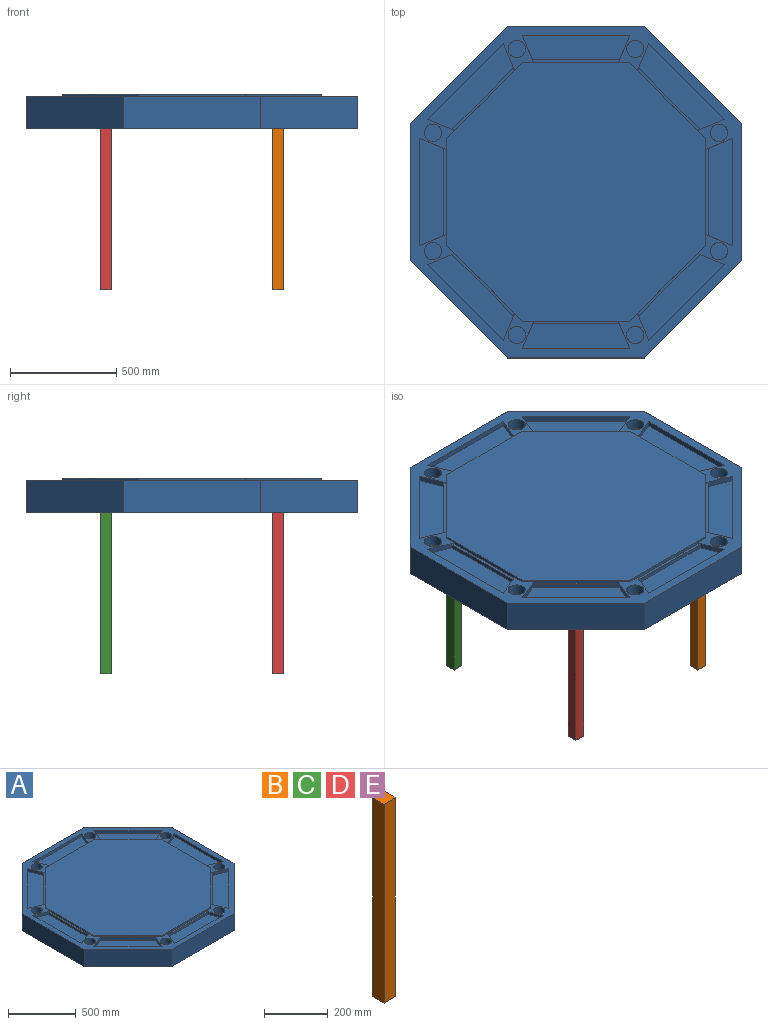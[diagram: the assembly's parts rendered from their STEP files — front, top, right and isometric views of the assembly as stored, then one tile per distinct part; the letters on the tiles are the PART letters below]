
ASSEMBLY  parts=5 mates=4
PART A: 84 faces, bbox 1564.9x1564.9x161.9 mm
  f0: plane 129.64x53.7mm, normal (-0.92,-0.38,0), area 3302.3mm2, adj f1,f9,f13,f61,f81,f83
  f1: plane 407.06x407.06mm, normal (0,0,1), area 53644.2mm2, adj f0,f13,f37,f81,f82
  f2: plane 129.64x53.7mm, normal (-0.38,-0.92,0), area 3302.3mm2, adj f9,f24,f60,f62,f79,f80
  f3: plane 407.06x407.06mm, normal (0,0,1), area 53644.1mm2, adj f10,f34,f35,f77
  f4: plane 129.64x53.7mm, normal (0.92,-0.38,0), area 3302.3mm2, adj f5,f9,f23,f58,f75,f76
  f5: plane 507.17x116.94mm, normal (0,0,1), area 53644.2mm2, adj f4,f23,f33,f75
  f6: plane 507.17x116.94mm, normal (0,0,1), area 53644.1mm2, adj f21,f29,f30,f71
  f7: plane 129.64x53.7mm, normal (-0.38,0.92,0), area 3302.3mm2, adj f9,f11,f55,f64,f69,f70
  f8: plane 129.64x53.7mm, normal (-0.92,0.38,0), area 3302.3mm2, adj f9,f12,f54,f65,f67,f68
  f9: plane 1564.91x1564.91mm, normal (0,0,1), area 285544.7mm2, adj f0,f2,f4,f7,f8,f10,f11,f12
  f10: plane 358.62x358.62mm, normal (0.71,0.71,0), area 12882mm2, adj f3,f9,f34,f35
  f11: plane 358.62x358.62mm, normal (-0.71,-0.71,0), area 12882mm2, adj f7,f9,f28,f64
  f12: plane 507.17x25.4mm, normal (0,-1,0), area 12882mm2, adj f8,f9,f27,f65
  f13: plane 358.62x358.62mm, normal (0.71,-0.71,0), area 12882mm2, adj f0,f1,f9,f37
  f14: plane 458.35x458.35mm, normal (-0.71,0.71,0), area 98786.8mm2, adj f9,f15,f25,f26
  f15: plane 648.21x152.4mm, normal (-1,0,0), area 98786.8mm2, adj f9,f14,f16,f26
  f16: plane 458.35x458.35mm, normal (-0.71,-0.71,0), area 98786.8mm2, adj f9,f15,f17,f26
  f17: plane 648.21x152.4mm, normal (0,-1,0), area 98786.8mm2, adj f9,f16,f18,f26
  f18: plane 458.35x458.35mm, normal (0.71,-0.71,0), area 98786.7mm2, adj f9,f17,f19,f26
  f19: plane 648.21x152.4mm, normal (1,0,0), area 98786.8mm2, adj f9,f18,f20,f26
  f20: plane 458.35x458.35mm, normal (0.71,0.71,0), area 98786.7mm2, adj f9,f19,f25,f26
  f21: plane 507.17x25.4mm, normal (-1,0,0), area 12882mm2, adj f6,f9,f29,f30
  f22: plane 358.62x358.62mm, normal (-0.71,0.71,0), area 12882mm2, adj f9,f31,f32,f63
  f23: plane 507.17x25.4mm, normal (0,1,0), area 12882mm2, adj f4,f5,f9,f33
  f24: plane 507.17x25.4mm, normal (1,0,0), area 12882mm2, adj f2,f9,f36,f62
  f25: plane 648.21x152.4mm, normal (0,1,0), area 98786.8mm2, adj f9,f14,f20,f26
  f26: plane 1564.91x1564.91mm, normal (0,0,-1), area 2028772.5mm2, adj f14,f15,f16,f17,f18,f19,f20,f25
  f27: plane 129.64x53.7mm, normal (0.92,0.38,0), area 3302.3mm2, adj f9,f12,f54,f65,f67,f68
  f28: plane 129.64x53.7mm, normal (0.92,-0.38,0), area 3302.3mm2, adj f9,f11,f55,f64,f69,f70
  f29: plane 129.64x53.7mm, normal (0.38,-0.92,0), area 3302.3mm2, adj f6,f9,f21,f56,f71,f72
  f30: plane 129.64x53.7mm, normal (0.38,0.92,0), area 3302.3mm2, adj f6,f9,f21,f56,f71,f72
  f31: plane 129.64x53.7mm, normal (-0.38,-0.92,0), area 3302.3mm2, adj f9,f22,f57,f63,f73,f74
  f32: plane 129.64x53.7mm, normal (0.92,0.38,0), area 3302.3mm2, adj f9,f22,f57,f63,f73,f74
  f33: plane 129.64x53.7mm, normal (-0.92,-0.38,0), area 3302.3mm2, adj f5,f9,f23,f58,f75,f76
  f34: plane 129.64x53.7mm, normal (-0.92,0.38,0), area 3302.3mm2, adj f3,f9,f10,f59,f77,f78
  f35: plane 129.64x53.7mm, normal (0.38,-0.92,0), area 3302.3mm2, adj f3,f9,f10,f59,f77,f78
  f36: plane 129.64x53.7mm, normal (-0.38,0.92,0), area 3302.3mm2, adj f9,f24,f60,f62,f79,f80
  f37: plane 129.64x53.7mm, normal (0.38,0.92,0), area 3302.3mm2, adj f1,f9,f13,f61,f82,f83
  f38: cylinder r=40.64mm len=81.28mm, axis (0,0,-1), area 12971.7mm2, adj f9,f53
  f39: cylinder r=40.64mm len=81.28mm, axis (0,0,-1), area 12971.7mm2, adj f9,f51
  f40: cylinder r=40.64mm len=81.28mm, axis (0,0,-1), area 12971.7mm2, adj f9,f49
  f41: cylinder r=40.64mm len=81.28mm, axis (0,0,-1), area 12971.7mm2, adj f9,f48
  f42: cylinder r=40.64mm len=81.28mm, axis (0,0,-1), area 12971.7mm2, adj f9,f52
  f43: cylinder r=40.64mm len=81.28mm, axis (0,0,-1), area 12971.7mm2, adj f9,f50
  f44: cylinder r=40.64mm len=81.28mm, axis (0,0,-1), area 12971.7mm2, adj f9,f47
  f45: cylinder r=40.64mm len=81.28mm, axis (0,0,-1), area 12971.7mm2, adj f9,f46
  f46: plane 81.28x81.28mm, normal (0,0,1), area 5188.7mm2, adj f45
  f47: plane 81.28x81.28mm, normal (0,0,1), area 5188.7mm2, adj f44
  f48: plane 81.28x81.28mm, normal (0,0,1), area 5188.7mm2, adj f41
  f49: plane 81.28x81.28mm, normal (0,0,1), area 5188.7mm2, adj f40
  f50: plane 81.28x81.28mm, normal (0,0,1), area 5188.7mm2, adj f43
  f51: plane 81.28x81.28mm, normal (0,0,1), area 5188.7mm2, adj f39
  f52: plane 81.28x81.28mm, normal (0,0,1), area 5188.7mm2, adj f42
  f53: plane 81.28x81.28mm, normal (0,0,1), area 5188.7mm2, adj f38
  f54: plane 505.01x15.88mm, normal (0,1,0), area 7348.7mm2, adj f8,f9,f27,f55,f61,f66,f68
  f55: plane 357.1x357.1mm, normal (0.71,0.71,0), area 7348.7mm2, adj f7,f9,f28,f54,f56,f66,f70
  f56: plane 505.01x15.88mm, normal (1,0,0), area 7348.7mm2, adj f9,f29,f30,f55,f57,f66,f72
  f57: plane 357.1x357.1mm, normal (0.71,-0.71,0), area 7348.7mm2, adj f9,f31,f32,f56,f58,f66,f74
  f58: plane 505.01x15.88mm, normal (0,-1,0), area 7348.7mm2, adj f4,f9,f33,f57,f59,f66,f76
  f59: plane 357.1x357.1mm, normal (-0.71,-0.71,0), area 7348.7mm2, adj f9,f34,f35,f58,f60,f66,f78
  f60: plane 505.01x15.88mm, normal (-1,0,0), area 7348.7mm2, adj f2,f9,f36,f59,f61,f66,f80
  f61: plane 357.1x357.1mm, normal (-0.71,0.71,0), area 7348.7mm2, adj f0,f9,f37,f54,f60,f66,f83
  f62: plane 507.17x116.94mm, normal (0,0,1), area 53644.1mm2, adj f2,f24,f36,f79
  f63: plane 407.06x407.06mm, normal (0,0,1), area 53644.2mm2, adj f22,f31,f32,f73
  f64: plane 407.06x407.06mm, normal (0,0,1), area 53644mm2, adj f7,f11,f28,f69
  f65: plane 507.17x116.94mm, normal (0,0,1), area 53644.1mm2, adj f8,f12,f27,f67
  f66: plane 1219.2x1219.2mm, normal (0,0,1), area 1231414.4mm2, adj f54,f55,f56,f57,f58,f59,f60,f61
  f67: plane 410.29x19.05mm, normal (0,1,0), area 7816mm2, adj f8,f27,f65,f68
  f68: plane 410.29x12.7mm, normal (0,0,1), area 5143.8mm2, adj f8,f27,f54,f67
  f69: plane 290.12x290.12mm, normal (0.71,0.71,0), area 7816mm2, adj f7,f28,f64,f70
  f70: plane 295.38x295.38mm, normal (0,0,1), area 5143.8mm2, adj f7,f28,f55,f69
  f71: plane 410.29x19.05mm, normal (1,0,0), area 7816mm2, adj f6,f29,f30,f72
  f72: plane 410.29x12.7mm, normal (0,0,1), area 5143.9mm2, adj f29,f30,f56,f71
  f73: plane 290.12x290.12mm, normal (0.71,-0.71,0), area 7816mm2, adj f31,f32,f63,f74
  f74: plane 295.38x295.38mm, normal (0,0,1), area 5143.8mm2, adj f31,f32,f57,f73
  f75: plane 410.29x19.05mm, normal (0,-1,0), area 7816mm2, adj f4,f5,f33,f76
  f76: plane 410.29x12.7mm, normal (0,0,1), area 5143.9mm2, adj f4,f33,f58,f75
  f77: plane 290.12x290.12mm, normal (-0.71,-0.71,0), area 7816mm2, adj f3,f34,f35,f78
  f78: plane 295.38x295.38mm, normal (0,0,1), area 5143.9mm2, adj f34,f35,f59,f77
  f79: plane 410.29x19.05mm, normal (-1,0,0), area 7816mm2, adj f2,f36,f62,f80
  f80: plane 410.29x12.7mm, normal (0,0,1), area 5143.9mm2, adj f2,f36,f60,f79
  f81: plane 290.12x290.12mm, normal (-0.71,0.71,0), area 7816mm2, adj f0,f1,f82,f83
  f82: plane 19.05x0mm, normal (0,1,0), area 0mm2, adj f1,f37,f81,f83
  f83: plane 295.38x295.38mm, normal (0,0,1), area 5143.9mm2, adj f0,f37,f61,f81,f82
PART B: 6 faces, bbox 50.8x50.8x762 mm
  f0: plane 50.8x50.8mm, normal (0,0,-1), area 2580.6mm2, adj f2,f3,f4,f5
  f1: plane 50.8x50.8mm, normal (0,0,1), area 2580.6mm2, adj f2,f3,f4,f5
  f2: plane 762x50.8mm, normal (-1,0,0), area 38709.6mm2, adj f0,f1,f3,f4
  f3: plane 762x50.8mm, normal (0,-1,0), area 38709.6mm2, adj f0,f1,f2,f5
  f4: plane 762x50.8mm, normal (0,1,0), area 38709.6mm2, adj f0,f1,f2,f5
  f5: plane 762x50.8mm, normal (1,0,0), area 38709.6mm2, adj f0,f1,f3,f4
PART C: same geometry as B
PART D: same geometry as B
PART E: same geometry as B
PLACE A t=(-3,0.59,18.22)mm fixed
PLACE B t=(403.4,-380.41,-819.98)mm
PLACE C rot(axis=(0.71,-0.71,0),180deg) t=(-434.8,406.99,-57.98)mm
PLACE D t=(-409.4,-380.41,-819.98)mm
PLACE E rot(axis=(1,0,0),180deg) t=(403.4,381.59,-57.98)mm
MATE fastened B.f1 <-> A.f26  axis (0,0,1) through (403.4,-405.81,-57.98)mm
MATE fastened E.f0 <-> A.f26  axis (0,0,1) through (403.4,406.99,-57.98)mm
MATE fastened C.f0 <-> A.f26  axis (0,0,1) through (-409.4,406.99,-57.98)mm
MATE fastened D.f1 <-> A.f26  axis (0,0,1) through (-409.4,-405.81,-57.98)mm
